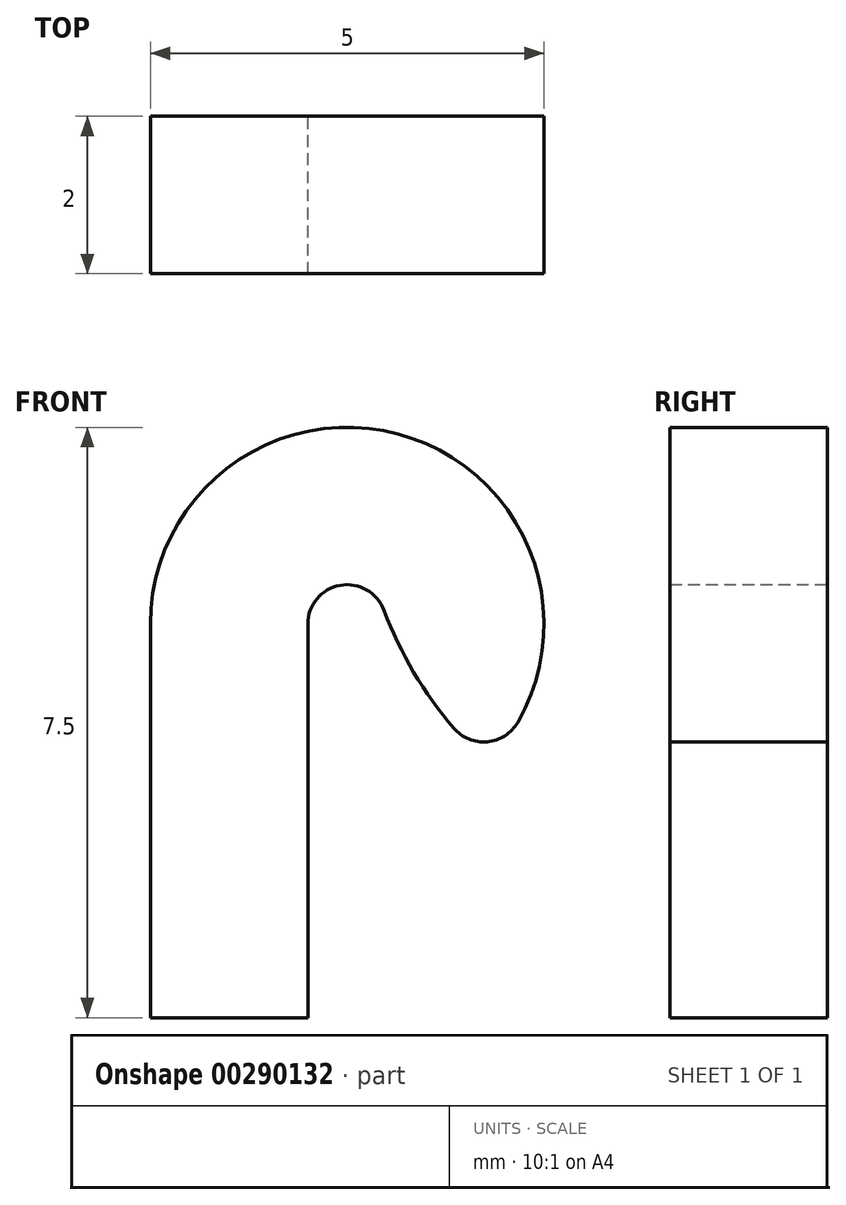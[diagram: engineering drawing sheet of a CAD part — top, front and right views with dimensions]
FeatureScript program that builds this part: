
annotation { "Feature Type Name" : "Feature", "Feature Type Description" : "" }
export const myFeature = defineFeature(function(context is Context, id is Id, definition is map)
    precondition{}
    {
        {
            var Q0;
            Q0=qCreatedBy(makeId("Front.planeOp"),FACE);
            var sketch = newSketch(context, id + "F0", { "sketchPlane" : qUnion([Q0])});
            skLineSegment(sketch, "E0.bottom", {"start": v(0, 0) * mm, "end": v(2, 0) * mm});
            skLineSegment(sketch, "E0.top", {"start": v(0, 5) * mm, "end": v(2, 5) * mm});
            skLineSegment(sketch, "E0.left", {"start": v(0, 0) * mm, "end": v(0, 5) * mm});
            skLineSegment(sketch, "E0.right", {"start": v(2, 0) * mm, "end": v(2, 5) * mm});
            skLineSegment(sketch, "E1", {"start": v(2, 5) * mm, "end": v(5, 5) * mm});
            skPoint(sketch, "E2", {"position": v(2.5, 5) * mm});
            skArc(sketch, "E3", {"start": v(0, 5) * mm, "mid": v(3.45, 7.31) * mm, "end": v(4.27, 3.24) * mm});
            skLineSegment(sketch, "E4", {"start": v(2.5, 5) * mm, "end": v(4.27, 3.24) * mm});
            skArc(sketch, "E5", {"start": v(2, 5) * mm, "mid": v(2.7, 5.46) * mm, "end": v(2.85, 4.65) * mm});
            skSolve(sketch);
        }
        {
            var Q0;
            Q0=makeQuery(id+"F0.imprint","IMPRINT",FACE,{"disambiguationData":[TD([[makeQuery(id+"F0.imprint","IMPRINT",EDGE,{"derivedFrom":sQuery(id+"F0.wireOp",EDGE,"E0.bottom")}),1.0]])]});
            var Q1;
            {var subQ0=sQuery(id+"F0.wireOp",EDGE,"E0.top");Q1=makeQuery(id+"F0.imprint","IMPRINT",FACE,{"disambiguationData":[TD([[makeQuery(id+"F0.imprint","IMPRINT",EDGE,{"derivedFrom":subQ0}),1.0]])]});}
            var Q2;
            {var subQ0=sQuery(id+"F0.wireOp",EDGE,"E3");var subQ1=sQuery(id+"F0.wireOp",EDGE,"E1");var subQ2=makeQuery(id+"F0.imprint","INTERSECT",VERTEX,{"derivedFrom":[subQ1,subQ0]});Q2=makeQuery(id+"F0.imprint","IMPRINT",FACE,{"disambiguationData":[TD([[makeQuery(id+"F0.imprint","IMPRINT",EDGE,{"disambiguationData":[TD([[subQ2,1.0]])],"derivedFrom":subQ1}),-1.0]])]});}
            extrude(context, id + "F1", {"entities" : qUnion([Q0, Q1, Q2]), "depth" : 2 * mm});
        }
        {
            var Q0;
            Q0=makeQuery(id+"F1.opExtrude","SWEPT_EDGE",EDGE,{"disambiguationData":[OSD([sQuery(id+"F0.wireOp",EDGE,"E4"),sQuery(id+"F0.wireOp",EDGE,"E5")])]});
            fillet(context, id + "F2", {"entities" : qUnion([Q0]), "radius" : 5 * mm, "tangentPropagation" : true, "allowEdgeOverflow" : false});
        }
        {
            var Q0;
            Q0=makeQuery(id+"F1.opExtrude","SWEPT_EDGE",EDGE,{"disambiguationData":[OSD([sQuery(id+"F0.wireOp",EDGE,"E3"),sQuery(id+"F0.wireOp",EDGE,"E4")])]});
            fillet(context, id + "F3", {"entities" : qUnion([Q0]), "radius" : .5 * mm, "tangentPropagation" : true, "allowEdgeOverflow" : false});
        }
    });
